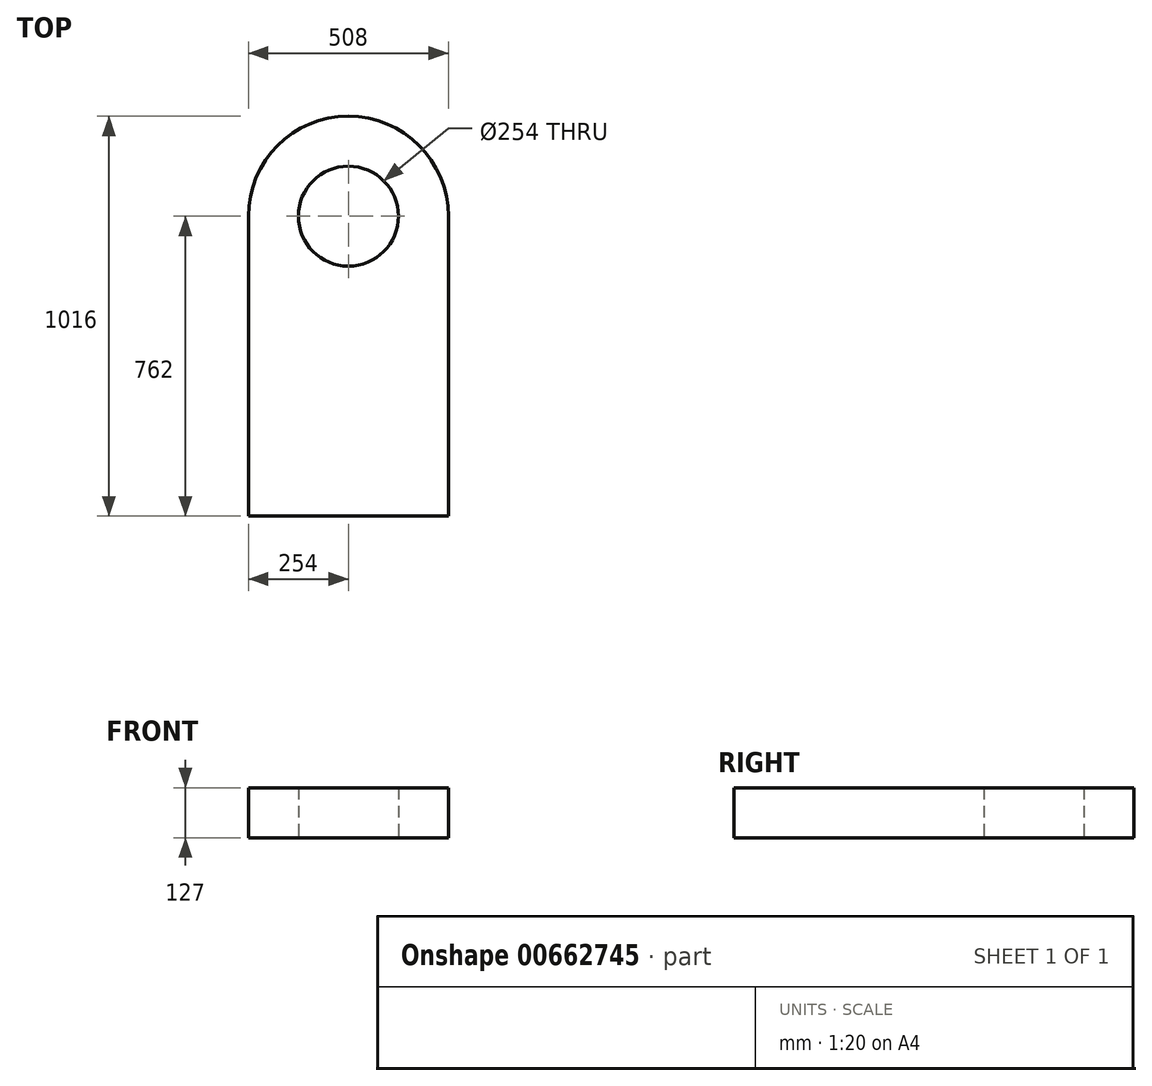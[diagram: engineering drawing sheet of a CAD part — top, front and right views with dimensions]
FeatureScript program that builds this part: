
annotation { "Feature Type Name" : "Feature", "Feature Type Description" : "" }
export const myFeature = defineFeature(function(context is Context, id is Id, definition is map)
    precondition{}
    {
        {
            var Q0;
            Q0=qCreatedBy(makeId("Top.planeOp"),FACE);
            var sketch = newSketch(context, id + "F0", { "sketchPlane" : qUnion([Q0])});
            skLineSegment(sketch, "E0.bottom", {"start": v(-254, 0) * mm, "end": v(254, 0) * mm, "construction": true});
            skLineSegment(sketch, "E0.top", {"start": v(-254, -762) * mm, "end": v(254, -762) * mm});
            skLineSegment(sketch, "E0.left", {"start": v(-254, 0) * mm, "end": v(-254, -762) * mm});
            skLineSegment(sketch, "E0.right", {"start": v(254, 0) * mm, "end": v(254, -762) * mm});
            skArc(sketch, "E1", {"start": v(254, 0) * mm, "mid": v(0, 254) * mm, "end": v(-254, 0) * mm});
            skCircle(sketch, "E2", {"center": v(0, 0) * mm, "radius": 127 * mm});
            skSolve(sketch);
        }
        {
            var Q0;
            Q0 = qSketchRegion(id + "F0", true);
            extrude(context, id + "F1", {"entities" : qUnion([Q0]), "depth" : 127 * mm, "offsetDistance" : 25.4 * mm});
        }
    });
